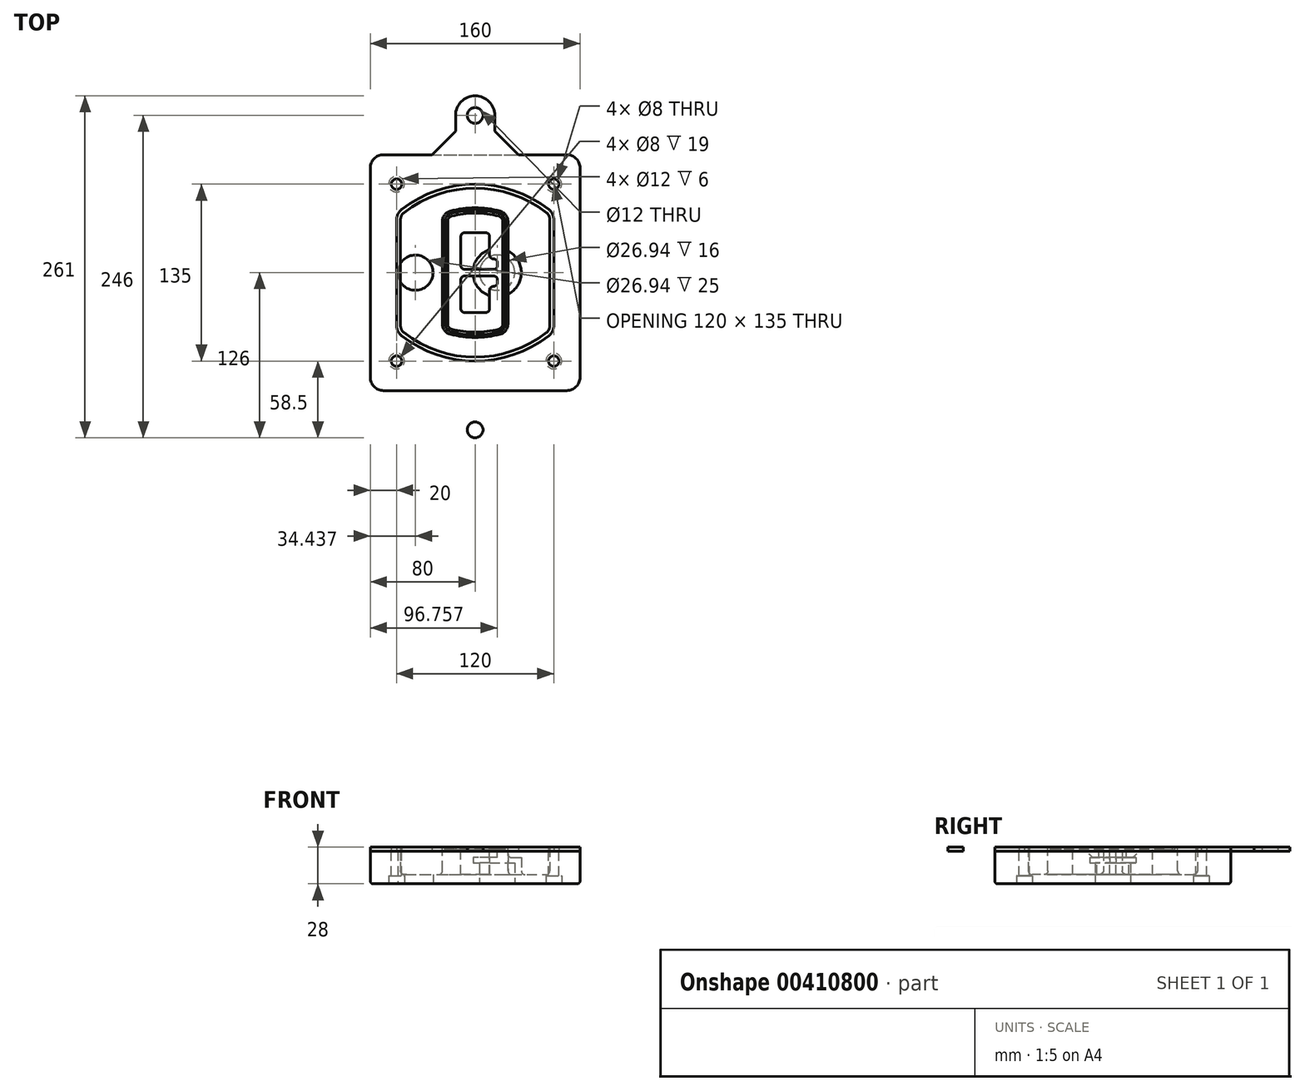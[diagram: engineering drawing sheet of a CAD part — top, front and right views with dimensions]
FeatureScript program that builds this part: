
annotation { "Feature Type Name" : "Feature", "Feature Type Description" : "" }
export const myFeature = defineFeature(function(context is Context, id is Id, definition is map)
    precondition{}
    {
        {
            var Q0;
            Q0=qCreatedBy(makeId("Top.planeOp"),FACE);
            var sketch = newSketch(context, id + "F0", { "sketchPlane" : qUnion([Q0])});
            skPoint(sketch, "E0.rect.middle", {"position": v(0, 0) * mm});
            skLineSegment(sketch, "E1.bottom", {"start": v(-70, -90) * mm, "end": v(70, -90) * mm});
            skLineSegment(sketch, "E1.top", {"start": v(-70, 90) * mm, "end": v(70, 90) * mm});
            skLineSegment(sketch, "E1.left", {"start": v(-80, -80) * mm, "end": v(-80, 80) * mm});
            skLineSegment(sketch, "E1.right", {"start": v(80, -80) * mm, "end": v(80, 80) * mm});
            skLineSegment(sketch, "E2", {"start": v(-80, 90) * mm, "end": v(80, -90) * mm, "construction": true});
            skLineSegment(sketch, "E3", {"start": v(80, 90) * mm, "end": v(-80, -90) * mm, "construction": true});
            skCircle(sketch, "E4", {"center": v(-60, 67.5) * mm, "radius": 4 * mm});
            skCircle(sketch, "E5", {"center": v(60, 67.5) * mm, "radius": 4 * mm});
            skCircle(sketch, "E6", {"center": v(60, -67.5) * mm, "radius": 4 * mm});
            skCircle(sketch, "E7", {"center": v(-60, -67.5) * mm, "radius": 4 * mm});
            skLineSegment(sketch, "E8", {"start": v(-60, 67.5) * mm, "end": v(60, 67.5) * mm, "construction": true});
            skLineSegment(sketch, "E9", {"start": v(60, 67.5) * mm, "end": v(60, -67.5) * mm, "construction": true});
            skLineSegment(sketch, "E10", {"start": v(60, -67.5) * mm, "end": v(-60, -67.5) * mm, "construction": true});
            skLineSegment(sketch, "E11", {"start": v(-60, -67.5) * mm, "end": v(-60, 67.5) * mm, "construction": true});
            skLineSegment(sketch, "E12", {"start": v(-60, 40.3) * mm, "end": v(-60, -40.3) * mm});
            skLineSegment(sketch, "E13", {"start": v(60, 40.3) * mm, "end": v(60, -40.3) * mm});
            skArc(sketch, "E14", {"start": v(56.15, 48.18) * mm, "mid": v(0, 67.5) * mm, "end": v(-56.15, 48.18) * mm});
            skArc(sketch, "E15", {"start": v(-56.15, -48.18) * mm, "mid": v(0, -67.5) * mm, "end": v(56.15, -48.18) * mm});
            skLineSegment(sketch, "E16", {"start": v(-60, 0) * mm, "end": v(60, 0) * mm, "construction": true});
            skPoint(sketch, "E17.visualSharp", {"position": v(-60, -45) * mm});
            skArc(sketch, "E17.filletArc", {"start": v(-60, -40.3) * mm, "mid": v(-58.99, -44.68) * mm, "end": v(-56.15, -48.18) * mm});
            skPoint(sketch, "E18.visualSharp", {"position": v(-60, 45) * mm});
            skArc(sketch, "E18.filletArc", {"start": v(-56.15, 48.18) * mm, "mid": v(-58.99, 44.68) * mm, "end": v(-60, 40.3) * mm});
            skPoint(sketch, "E19.visualSharp", {"position": v(60, 45) * mm});
            skArc(sketch, "E19.filletArc", {"start": v(60, 40.3) * mm, "mid": v(58.99, 44.68) * mm, "end": v(56.15, 48.18) * mm});
            skPoint(sketch, "E20.visualSharp", {"position": v(60, -45) * mm});
            skArc(sketch, "E20.filletArc", {"start": v(56.15, -48.18) * mm, "mid": v(58.99, -44.68) * mm, "end": v(60, -40.3) * mm});
            skPoint(sketch, "E21.visualSharp", {"position": v(-80, 90) * mm});
            skArc(sketch, "E21.filletArc", {"start": v(-70, 90) * mm, "mid": v(-77.07, 87.07) * mm, "end": v(-80, 80) * mm});
            skPoint(sketch, "E22.visualSharp", {"position": v(80, 90) * mm});
            skArc(sketch, "E22.filletArc", {"start": v(80, 80) * mm, "mid": v(77.07, 87.07) * mm, "end": v(70, 90) * mm});
            skPoint(sketch, "E23.visualSharp", {"position": v(80, -90) * mm});
            skArc(sketch, "E23.filletArc", {"start": v(70, -90) * mm, "mid": v(77.07, -87.07) * mm, "end": v(80, -80) * mm});
            skPoint(sketch, "E24.visualSharp", {"position": v(-80, -90) * mm});
            skArc(sketch, "E24.filletArc", {"start": v(-80, -80) * mm, "mid": v(-77.07, -87.07) * mm, "end": v(-70, -90) * mm});
            skArc(sketch, "E25.0", {"start": v(57, 40.3) * mm, "mid": v(56.3, 43.36) * mm, "end": v(54.3, 45.81) * mm});
            skLineSegment(sketch, "E25.1", {"start": v(57, 40.3) * mm, "end": v(57, -40.3) * mm});
            skArc(sketch, "E25.2", {"start": v(54.3, -45.81) * mm, "mid": v(56.3, -43.36) * mm, "end": v(57, -40.3) * mm});
            skArc(sketch, "E25.3", {"start": v(-54.3, -45.81) * mm, "mid": v(0, -64.5) * mm, "end": v(54.3, -45.81) * mm});
            skArc(sketch, "E25.4", {"start": v(-57, -40.3) * mm, "mid": v(-56.3, -43.36) * mm, "end": v(-54.3, -45.81) * mm});
            skArc(sketch, "E25.5", {"start": v(54.3, 45.81) * mm, "mid": v(0, 64.5) * mm, "end": v(-54.3, 45.81) * mm});
            skLineSegment(sketch, "E25.6", {"start": v(-57, 40.3) * mm, "end": v(-57, -40.3) * mm});
            skArc(sketch, "E25.7", {"start": v(-54.3, 45.81) * mm, "mid": v(-56.3, 43.36) * mm, "end": v(-57, 40.3) * mm});
            skArc(sketch, "E26.0", {"start": v(-58.62, 51.33) * mm, "mid": v(-62.58, 46.43) * mm, "end": v(-64, 40.3) * mm});
            skArc(sketch, "E26.1", {"start": v(58.62, 51.33) * mm, "mid": v(0, 71.5) * mm, "end": v(-58.62, 51.33) * mm});
            skArc(sketch, "E26.2", {"start": v(64, 40.3) * mm, "mid": v(62.58, 46.43) * mm, "end": v(58.62, 51.33) * mm});
            skLineSegment(sketch, "E26.3", {"start": v(64, 40.3) * mm, "end": v(64, -40.3) * mm});
            skArc(sketch, "E26.4", {"start": v(58.62, -51.33) * mm, "mid": v(62.58, -46.43) * mm, "end": v(64, -40.3) * mm});
            skLineSegment(sketch, "E26.5", {"start": v(-64, 40.3) * mm, "end": v(-64, -40.3) * mm});
            skArc(sketch, "E26.6", {"start": v(-58.62, -51.33) * mm, "mid": v(0, -71.5) * mm, "end": v(58.62, -51.33) * mm});
            skArc(sketch, "E26.7", {"start": v(-64, -40.3) * mm, "mid": v(-62.58, -46.43) * mm, "end": v(-58.62, -51.33) * mm});
            skSolve(sketch);
        }
        {
            var Q0;
            Q0=makeQuery(id+"F0.imprint","IMPRINT",FACE,{"disambiguationData":[TD([[makeQuery(id+"F0.imprint","IMPRINT",EDGE,{"derivedFrom":sQuery(id+"F0.wireOp",EDGE,"E1.bottom")}),1.0]])]});
            var Q1;
            Q1=makeQuery(id+"F0.imprint","IMPRINT",FACE,{"disambiguationData":[TD([[makeQuery(id+"F0.imprint","IMPRINT",EDGE,{"derivedFrom":sQuery(id+"F0.wireOp",EDGE,"E12")}),1.0]])]});
            var Q2;
            Q2=makeQuery(id+"F0.imprint","IMPRINT",FACE,{"disambiguationData":[TD([[makeQuery(id+"F0.imprint","IMPRINT",EDGE,{"derivedFrom":sQuery(id+"F0.wireOp",EDGE,"E25.0")}),1.0]])]});
            var Q3;
            Q3=makeQuery(id+"F0.imprint","IMPRINT",FACE,{"disambiguationData":[TD([[makeQuery(id+"F0.imprint","IMPRINT",EDGE,{"derivedFrom":sQuery(id+"F0.wireOp",EDGE,"E12")}),-1.0]])]});
            extrude(context, id + "F1", {"entities" : qUnion([Q0, Q1, Q2, Q3]), "oppositeDirection" : true, "depth" : 25 * mm});
        }
        {
            var Q0;
            Q0=makeQuery(id+"F0.imprint","IMPRINT",FACE,{"disambiguationData":[TD([[makeQuery(id+"F0.imprint","IMPRINT",EDGE,{"derivedFrom":sQuery(id+"F0.wireOp",EDGE,"E12")}),1.0]])]});
            extrude(context, id + "F2", {"entities" : qUnion([Q0]), "operationType" : NewBodyOperationType.ADD, "depth" : 3 * mm});
        }
        {
            var Q0;
            Q0=makeQuery(id+"F0.imprint","IMPRINT",FACE,{"disambiguationData":[TD([[makeQuery(id+"F0.imprint","IMPRINT",EDGE,{"derivedFrom":sQuery(id+"F0.wireOp",EDGE,"E25.0")}),1.0]])]});
            extrude(context, id + "F3", {"entities" : qUnion([Q0]), "operationType" : NewBodyOperationType.REMOVE, "oppositeDirection" : true, "depth" : 18 * mm});
        }
        {
            var Q0;
            Q0=makeQuery(id+"F2.opExtrude","CAP_FACE",FACE,{"disambiguationData":[OSD([sQuery(id+"F0.wireOp",EDGE,"E12"),sQuery(id+"F0.wireOp",EDGE,"E13"),sQuery(id+"F0.wireOp",EDGE,"E14"),sQuery(id+"F0.wireOp",EDGE,"E15"),sQuery(id+"F0.wireOp",EDGE,"E17.filletArc"),sQuery(id+"F0.wireOp",EDGE,"E18.filletArc"),sQuery(id+"F0.wireOp",EDGE,"E19.filletArc"),sQuery(id+"F0.wireOp",EDGE,"E20.filletArc"),sQuery(id+"F0.wireOp",EDGE,"E25.0"),sQuery(id+"F0.wireOp",EDGE,"E25.1"),sQuery(id+"F0.wireOp",EDGE,"E25.2"),sQuery(id+"F0.wireOp",EDGE,"E25.3"),sQuery(id+"F0.wireOp",EDGE,"E25.4"),sQuery(id+"F0.wireOp",EDGE,"E25.5"),sQuery(id+"F0.wireOp",EDGE,"E25.6"),sQuery(id+"F0.wireOp",EDGE,"E25.7")])],"isStart":false});
            var sketch = newSketch(context, id + "F4", { "sketchPlane" : qUnion([Q0])});
            skArc(sketch, "E27.0", {"start": v(-19.08, -46.97) * mm, "mid": v(0, -49.5) * mm, "end": v(19.08, -46.97) * mm});
            skArc(sketch, "E28.0", {"start": v(19.08, 46.97) * mm, "mid": v(0, 49.5) * mm, "end": v(-19.08, 46.97) * mm});
            skLineSegment(sketch, "E29", {"start": v(-25, 39.25) * mm, "end": v(-25, -39.25) * mm});
            skLineSegment(sketch, "E30", {"start": v(25, 39.25) * mm, "end": v(25, -39.25) * mm});
            skLineSegment(sketch, "E31", {"start": v(-25, 45.1) * mm, "end": v(25, 45.1) * mm, "construction": true});
            skLineSegment(sketch, "E32", {"start": v(-25, -45.1) * mm, "end": v(25, -45.1) * mm, "construction": true});
            skPoint(sketch, "E33.visualSharp", {"position": v(-25, 45.1) * mm});
            skArc(sketch, "E33.filletArc", {"start": v(-19.08, 46.97) * mm, "mid": v(-23.35, 44.11) * mm, "end": v(-25, 39.25) * mm});
            skPoint(sketch, "E34.visualSharp", {"position": v(25, 45.1) * mm});
            skArc(sketch, "E34.filletArc", {"start": v(25, 39.25) * mm, "mid": v(23.35, 44.11) * mm, "end": v(19.08, 46.97) * mm});
            skPoint(sketch, "E35.visualSharp", {"position": v(25, -45.1) * mm});
            skArc(sketch, "E35.filletArc", {"start": v(19.08, -46.97) * mm, "mid": v(23.35, -44.11) * mm, "end": v(25, -39.25) * mm});
            skPoint(sketch, "E36.visualSharp", {"position": v(-25, -45.1) * mm});
            skArc(sketch, "E36.filletArc", {"start": v(-25, -39.25) * mm, "mid": v(-23.35, -44.11) * mm, "end": v(-19.08, -46.97) * mm});
            skArc(sketch, "E37.0", {"start": v(54.3, 45.81) * mm, "mid": v(0, 64.5) * mm, "end": v(-54.3, 45.81) * mm});
            skArc(sketch, "E37.1", {"start": v(-54.3, 45.81) * mm, "mid": v(-56.3, 43.36) * mm, "end": v(-57, 40.3) * mm});
            skLineSegment(sketch, "E37.2", {"start": v(-57, 40.3) * mm, "end": v(-57, -40.3) * mm});
            skArc(sketch, "E37.3", {"start": v(-57, -40.3) * mm, "mid": v(-56.3, -43.36) * mm, "end": v(-54.3, -45.81) * mm});
            skArc(sketch, "E37.4", {"start": v(-54.3, -45.81) * mm, "mid": v(0, -64.5) * mm, "end": v(54.3, -45.81) * mm});
            skArc(sketch, "E37.5", {"start": v(54.3, -45.81) * mm, "mid": v(56.3, -43.36) * mm, "end": v(57, -40.3) * mm});
            skLineSegment(sketch, "E37.6", {"start": v(57, 40.3) * mm, "end": v(57, -40.3) * mm});
            skArc(sketch, "E37.7", {"start": v(57, 40.3) * mm, "mid": v(56.3, 43.36) * mm, "end": v(54.3, 45.81) * mm});
            skLineSegment(sketch, "E38.0", {"start": v(23, 39.25) * mm, "end": v(23, -39.25) * mm});
            skArc(sketch, "E38.1", {"start": v(18.56, -45.04) * mm, "mid": v(21.76, -42.9) * mm, "end": v(23, -39.25) * mm});
            skArc(sketch, "E38.2", {"start": v(-18.56, -45.04) * mm, "mid": v(0, -47.5) * mm, "end": v(18.56, -45.04) * mm});
            skArc(sketch, "E38.3", {"start": v(-23, -39.25) * mm, "mid": v(-21.76, -42.9) * mm, "end": v(-18.56, -45.04) * mm});
            skLineSegment(sketch, "E38.4", {"start": v(-23, 39.25) * mm, "end": v(-23, -39.25) * mm});
            skArc(sketch, "E38.5", {"start": v(23, 39.25) * mm, "mid": v(21.76, 42.9) * mm, "end": v(18.56, 45.04) * mm});
            skArc(sketch, "E38.6", {"start": v(-18.56, 45.04) * mm, "mid": v(-21.76, 42.9) * mm, "end": v(-23, 39.25) * mm});
            skArc(sketch, "E38.7", {"start": v(18.56, 45.04) * mm, "mid": v(0, 47.5) * mm, "end": v(-18.56, 45.04) * mm});
            skArc(sketch, "E39.0", {"start": v(21, 39.25) * mm, "mid": v(20.18, 41.68) * mm, "end": v(18.04, 43.1) * mm});
            skLineSegment(sketch, "E39.1", {"start": v(21, 39.25) * mm, "end": v(21, -39.25) * mm});
            skArc(sketch, "E39.2", {"start": v(18.04, -43.1) * mm, "mid": v(20.18, -41.68) * mm, "end": v(21, -39.25) * mm});
            skArc(sketch, "E39.3", {"start": v(-18.04, -43.1) * mm, "mid": v(0, -45.5) * mm, "end": v(18.04, -43.1) * mm});
            skArc(sketch, "E39.4", {"start": v(-21, -39.25) * mm, "mid": v(-20.18, -41.68) * mm, "end": v(-18.04, -43.1) * mm});
            skArc(sketch, "E39.5", {"start": v(18.04, 43.1) * mm, "mid": v(0, 45.5) * mm, "end": v(-18.04, 43.1) * mm});
            skLineSegment(sketch, "E39.6", {"start": v(-21, 39.25) * mm, "end": v(-21, -39.25) * mm});
            skArc(sketch, "E39.7", {"start": v(-18.04, 43.1) * mm, "mid": v(-20.18, 41.68) * mm, "end": v(-21, 39.25) * mm});
            skLineSegment(sketch, "E40", {"start": v(-25, 0) * mm, "end": v(25, 0) * mm, "construction": true});
            skLineSegment(sketch, "E41", {"start": v(-11, 5.5) * mm, "end": v(-11, 27.5) * mm});
            skLineSegment(sketch, "E42", {"start": v(-8, 30.5) * mm, "end": v(8, 30.5) * mm});
            skLineSegment(sketch, "E43", {"start": v(11, 27.5) * mm, "end": v(11, 13.5) * mm});
            skLineSegment(sketch, "E44", {"start": v(14, 10.5) * mm, "end": v(14, 10.5) * mm});
            skLineSegment(sketch, "E45", {"start": v(17, 7.5) * mm, "end": v(17, 5.5) * mm});
            skLineSegment(sketch, "E46", {"start": v(14, 2.5) * mm, "end": v(-8, 2.5) * mm});
            skPoint(sketch, "E47.visualSharp", {"position": v(-11, 30.5) * mm});
            skArc(sketch, "E47.filletArc", {"start": v(-8, 30.5) * mm, "mid": v(-10.12, 29.62) * mm, "end": v(-11, 27.5) * mm});
            skPoint(sketch, "E48.visualSharp", {"position": v(11, 30.5) * mm});
            skArc(sketch, "E48.filletArc", {"start": v(11, 27.5) * mm, "mid": v(10.12, 29.62) * mm, "end": v(8, 30.5) * mm});
            skPoint(sketch, "E49.visualSharp", {"position": v(11, 10.5) * mm});
            skArc(sketch, "E49.filletArc", {"start": v(11, 13.5) * mm, "mid": v(11.88, 11.38) * mm, "end": v(14, 10.5) * mm});
            skPoint(sketch, "E50.visualSharp", {"position": v(17, 10.5) * mm});
            skArc(sketch, "E50.filletArc", {"start": v(17, 7.5) * mm, "mid": v(16.12, 9.62) * mm, "end": v(14, 10.5) * mm});
            skPoint(sketch, "E51.visualSharp", {"position": v(17, 2.5) * mm});
            skArc(sketch, "E51.filletArc", {"start": v(14, 2.5) * mm, "mid": v(16.12, 3.38) * mm, "end": v(17, 5.5) * mm});
            skPoint(sketch, "E52.visualSharp", {"position": v(-11, 2.5) * mm});
            skArc(sketch, "E52.filletArc", {"start": v(-11, 5.5) * mm, "mid": v(-10.12, 3.38) * mm, "end": v(-8, 2.5) * mm});
            skLineSegment(sketch, "E53.0.MirrorCS", {"start": v(14, -2.5) * mm, "end": v(-8, -2.5) * mm});
            skArc(sketch, "E54.0.MirrorCS", {"start": v(-11, -5.5) * mm, "mid": v(-10.12, -3.38) * mm, "end": v(-8, -2.5) * mm});
            skLineSegment(sketch, "E55.0.MirrorCS", {"start": v(-11, -5.5) * mm, "end": v(-11, -27.5) * mm});
            skArc(sketch, "E56.0.MirrorCS", {"start": v(-8, -30.5) * mm, "mid": v(-10.12, -29.62) * mm, "end": v(-11, -27.5) * mm});
            skLineSegment(sketch, "E57.0.MirrorCS", {"start": v(-8, -30.5) * mm, "end": v(8, -30.5) * mm});
            skArc(sketch, "E58.0.MirrorCS", {"start": v(11, -27.5) * mm, "mid": v(10.12, -29.62) * mm, "end": v(8, -30.5) * mm});
            skLineSegment(sketch, "E59.0.MirrorCS", {"start": v(11, -27.5) * mm, "end": v(11, -13.5) * mm});
            skArc(sketch, "E60.0.MirrorCS", {"start": v(11, -13.5) * mm, "mid": v(11.88, -11.38) * mm, "end": v(14, -10.5) * mm});
            skArc(sketch, "E61.0.MirrorCS", {"start": v(17, -7.5) * mm, "mid": v(16.12, -9.62) * mm, "end": v(14, -10.5) * mm});
            skLineSegment(sketch, "E62.0.MirrorCS", {"start": v(17, -7.5) * mm, "end": v(17, -5.5) * mm});
            skArc(sketch, "E63.0.MirrorCS", {"start": v(14, -2.5) * mm, "mid": v(16.12, -3.38) * mm, "end": v(17, -5.5) * mm});
            skSolve(sketch);
        }
        {
            var Q0;
            Q0=makeQuery(id+"F4.imprint","IMPRINT",FACE,{"disambiguationData":[TD([[makeQuery(id+"F4.imprint","IMPRINT",EDGE,{"derivedFrom":sQuery(id+"F4.wireOp",EDGE,"E27.0")}),1.0]])]});
            var Q1;
            Q1=makeQuery(id+"F4.imprint","IMPRINT",FACE,{"disambiguationData":[TD([[makeQuery(id+"F4.imprint","IMPRINT",EDGE,{"derivedFrom":sQuery(id+"F4.wireOp",EDGE,"E38.0")}),-1.0]])]});
            var Q2;
            Q2=makeQuery(id+"F4.imprint","IMPRINT",FACE,{"disambiguationData":[TD([[makeQuery(id+"F4.imprint","IMPRINT",EDGE,{"derivedFrom":sQuery(id+"F4.wireOp",EDGE,"E39.0")}),1.0]])]});
            extrude(context, id + "F5", {"entities" : qUnion([Q0, Q1, Q2]), "operationType" : NewBodyOperationType.ADD, "endBound" : BoundingType.UP_TO_NEXT, "oppositeDirection" : true, "depth" : 25 * mm});
        }
        {
            var Q0;
            Q0=makeQuery(id+"F4.imprint","IMPRINT",FACE,{"disambiguationData":[TD([[makeQuery(id+"F4.imprint","IMPRINT",EDGE,{"derivedFrom":sQuery(id+"F4.wireOp",EDGE,"E38.0")}),-1.0]])]});
            extrude(context, id + "F6", {"entities" : qUnion([Q0]), "operationType" : NewBodyOperationType.REMOVE, "oppositeDirection" : true, "depth" : 2 * mm});
        }
        {
            var Q0;
            Q0=makeQuery(id+"F1.opExtrude","CAP_FACE",FACE,{"disambiguationData":[OSD([sQuery(id+"F0.wireOp",EDGE,"E1.bottom"),sQuery(id+"F0.wireOp",EDGE,"E1.top"),sQuery(id+"F0.wireOp",EDGE,"E1.left"),sQuery(id+"F0.wireOp",EDGE,"E1.right"),sQuery(id+"F0.wireOp",EDGE,"E4"),sQuery(id+"F0.wireOp",EDGE,"E5"),sQuery(id+"F0.wireOp",EDGE,"E6"),sQuery(id+"F0.wireOp",EDGE,"E7"),sQuery(id+"F0.wireOp",EDGE,"E21.filletArc"),sQuery(id+"F0.wireOp",EDGE,"E22.filletArc"),sQuery(id+"F0.wireOp",EDGE,"E23.filletArc"),sQuery(id+"F0.wireOp",EDGE,"E24.filletArc")])],"isStart":false});
            var sketch = newSketch(context, id + "F7", { "sketchPlane" : qUnion([Q0])});
            skCircle(sketch, "E64", {"center": v(16.76, 0) * mm, "radius": 13.47 * mm});
            skCircle(sketch, "E65", {"center": v(-45.56, 0) * mm, "radius": 13.47 * mm});
            skLineSegment(sketch, "E66", {"start": v(80, 0) * mm, "end": v(-80, 0) * mm});
            skCircle(sketch, "E67", {"center": v(16.76, 0) * mm, "radius": 18.47 * mm});
            skCircle(sketch, "E68", {"center": v(60, -67.5) * mm, "radius": 6 * mm});
            skCircle(sketch, "E69", {"center": v(-60, -67.5) * mm, "radius": 6 * mm});
            skCircle(sketch, "E70", {"center": v(-60, 67.5) * mm, "radius": 6 * mm});
            skCircle(sketch, "E71", {"center": v(60, 67.5) * mm, "radius": 6 * mm});
            skSolve(sketch);
        }
        {
            var Q0;
            {var subQ1=sQuery(id+"F7.wireOp",EDGE,"E66");var subQ4=sQuery(id+"F7.wireOp",EDGE,"E64");var subQ6=makeQuery(id+"F7.imprint","INTERSECT",VERTEX,{"disambiguationData":[OD(0.0)],"derivedFrom":[subQ4,subQ1]});Q0=makeQuery(id+"F7.imprint","IMPRINT",FACE,{"disambiguationData":[TD([[makeQuery(id+"F7.imprint","IMPRINT",EDGE,{"disambiguationData":[TD([[subQ6,-1.0]])],"derivedFrom":subQ4}),-1.0]])]});}
            var Q1;
            {var subQ0=sQuery(id+"F7.wireOp",EDGE,"E66");var subQ1=sQuery(id+"F7.wireOp",EDGE,"E64");var subQ3=makeQuery(id+"F7.imprint","INTERSECT",VERTEX,{"disambiguationData":[OD(0.0)],"derivedFrom":[subQ1,subQ0]});Q1=makeQuery(id+"F7.imprint","IMPRINT",FACE,{"disambiguationData":[TD([[makeQuery(id+"F7.imprint","IMPRINT",EDGE,{"disambiguationData":[TD([[subQ3,-1.0]])],"derivedFrom":subQ1}),1.0]])]});}
            var Q2;
            {var subQ0=sQuery(id+"F7.wireOp",EDGE,"E66");var subQ1=sQuery(id+"F7.wireOp",EDGE,"E64");var subQ3=makeQuery(id+"F7.imprint","INTERSECT",VERTEX,{"disambiguationData":[OD(0.0)],"derivedFrom":[subQ1,subQ0]});Q2=makeQuery(id+"F7.imprint","IMPRINT",FACE,{"disambiguationData":[TD([[makeQuery(id+"F7.imprint","IMPRINT",EDGE,{"disambiguationData":[TD([[subQ3,1.0]])],"derivedFrom":subQ1}),1.0]])]});}
            var Q3;
            {var subQ1=sQuery(id+"F7.wireOp",EDGE,"E66");var subQ4=sQuery(id+"F7.wireOp",EDGE,"E64");var subQ6=makeQuery(id+"F7.imprint","INTERSECT",VERTEX,{"disambiguationData":[OD(0.0)],"derivedFrom":[subQ4,subQ1]});Q3=makeQuery(id+"F7.imprint","IMPRINT",FACE,{"disambiguationData":[TD([[makeQuery(id+"F7.imprint","IMPRINT",EDGE,{"disambiguationData":[TD([[subQ6,1.0]])],"derivedFrom":subQ4}),-1.0]])]});}
            extrude(context, id + "F8", {"entities" : qUnion([Q0, Q1, Q2, Q3]), "operationType" : NewBodyOperationType.ADD, "oppositeDirection" : true, "depth" : 20 * mm});
        }
        {
            var Q0;
            {var subQ0=sQuery(id+"F7.wireOp",EDGE,"E66");var subQ1=sQuery(id+"F7.wireOp",EDGE,"E64");var subQ3=makeQuery(id+"F7.imprint","INTERSECT",VERTEX,{"disambiguationData":[OD(0.0)],"derivedFrom":[subQ1,subQ0]});Q0=makeQuery(id+"F7.imprint","IMPRINT",FACE,{"disambiguationData":[TD([[makeQuery(id+"F7.imprint","IMPRINT",EDGE,{"disambiguationData":[TD([[subQ3,-1.0]])],"derivedFrom":subQ1}),1.0]])]});}
            var Q1;
            {var subQ0=sQuery(id+"F7.wireOp",EDGE,"E66");var subQ1=sQuery(id+"F7.wireOp",EDGE,"E64");var subQ3=makeQuery(id+"F7.imprint","INTERSECT",VERTEX,{"disambiguationData":[OD(0.0)],"derivedFrom":[subQ1,subQ0]});Q1=makeQuery(id+"F7.imprint","IMPRINT",FACE,{"disambiguationData":[TD([[makeQuery(id+"F7.imprint","IMPRINT",EDGE,{"disambiguationData":[TD([[subQ3,1.0]])],"derivedFrom":subQ1}),1.0]])]});}
            extrude(context, id + "F9", {"entities" : qUnion([Q0, Q1]), "operationType" : NewBodyOperationType.REMOVE, "oppositeDirection" : true, "depth" : 16 * mm});
        }
        {
            var Q0;
            {var subQ0=sQuery(id+"F7.wireOp",EDGE,"E66");var subQ1=sQuery(id+"F7.wireOp",EDGE,"E65");var subQ3=makeQuery(id+"F7.imprint","INTERSECT",VERTEX,{"disambiguationData":[OD(0.0)],"derivedFrom":[subQ1,subQ0]});Q0=makeQuery(id+"F7.imprint","IMPRINT",FACE,{"disambiguationData":[TD([[makeQuery(id+"F7.imprint","IMPRINT",EDGE,{"disambiguationData":[TD([[subQ3,-1.0]])],"derivedFrom":subQ1}),1.0]])]});}
            var Q1;
            {var subQ0=sQuery(id+"F7.wireOp",EDGE,"E66");var subQ1=sQuery(id+"F7.wireOp",EDGE,"E65");var subQ3=makeQuery(id+"F7.imprint","INTERSECT",VERTEX,{"disambiguationData":[OD(0.0)],"derivedFrom":[subQ1,subQ0]});Q1=makeQuery(id+"F7.imprint","IMPRINT",FACE,{"disambiguationData":[TD([[makeQuery(id+"F7.imprint","IMPRINT",EDGE,{"disambiguationData":[TD([[subQ3,1.0]])],"derivedFrom":subQ1}),1.0]])]});}
            extrude(context, id + "F10", {"entities" : qUnion([Q0, Q1]), "operationType" : NewBodyOperationType.REMOVE, "oppositeDirection" : true, "depth" : 25 * mm});
        }
        {
            var Q0;
            Q0=makeQuery(id+"F7.imprint","IMPRINT",FACE,{"disambiguationData":[TD([[makeQuery(id+"F7.imprint","IMPRINT",EDGE,{"derivedFrom":sQuery(id+"F7.wireOp",EDGE,"E68")}),1.0]])]});
            var Q1;
            Q1=makeQuery(id+"F7.imprint","IMPRINT",FACE,{"disambiguationData":[TD([[makeQuery(id+"F7.imprint","IMPRINT",EDGE,{"derivedFrom":makeQuery(id+"F1.opExtrude","CAP_EDGE",EDGE,{"disambiguationData":[OSD([sQuery(id+"F0.wireOp",EDGE,"E5")])],"isStart":false})}),-1.0]])]});
            var Q2;
            Q2=makeQuery(id+"F7.imprint","IMPRINT",FACE,{"disambiguationData":[TD([[makeQuery(id+"F7.imprint","IMPRINT",EDGE,{"derivedFrom":sQuery(id+"F7.wireOp",EDGE,"E69")}),1.0]])]});
            var Q3;
            Q3=makeQuery(id+"F7.imprint","IMPRINT",FACE,{"disambiguationData":[TD([[makeQuery(id+"F7.imprint","IMPRINT",EDGE,{"derivedFrom":makeQuery(id+"F1.opExtrude","CAP_EDGE",EDGE,{"disambiguationData":[OSD([sQuery(id+"F0.wireOp",EDGE,"E4")])],"isStart":false})}),-1.0]])]});
            var Q4;
            Q4=makeQuery(id+"F7.imprint","IMPRINT",FACE,{"disambiguationData":[TD([[makeQuery(id+"F7.imprint","IMPRINT",EDGE,{"derivedFrom":sQuery(id+"F7.wireOp",EDGE,"E70")}),1.0]])]});
            var Q5;
            Q5=makeQuery(id+"F7.imprint","IMPRINT",FACE,{"disambiguationData":[TD([[makeQuery(id+"F7.imprint","IMPRINT",EDGE,{"derivedFrom":makeQuery(id+"F1.opExtrude","CAP_EDGE",EDGE,{"disambiguationData":[OSD([sQuery(id+"F0.wireOp",EDGE,"E7")])],"isStart":false})}),-1.0]])]});
            var Q6;
            Q6=makeQuery(id+"F7.imprint","IMPRINT",FACE,{"disambiguationData":[TD([[makeQuery(id+"F7.imprint","IMPRINT",EDGE,{"derivedFrom":sQuery(id+"F7.wireOp",EDGE,"E71")}),1.0]])]});
            var Q7;
            Q7=makeQuery(id+"F7.imprint","IMPRINT",FACE,{"disambiguationData":[TD([[makeQuery(id+"F7.imprint","IMPRINT",EDGE,{"derivedFrom":makeQuery(id+"F1.opExtrude","CAP_EDGE",EDGE,{"disambiguationData":[OSD([sQuery(id+"F0.wireOp",EDGE,"E6")])],"isStart":false})}),-1.0]])]});
            extrude(context, id + "F11", {"entities" : qUnion([Q0, Q1, Q2, Q3, Q4, Q5, Q6, Q7]), "operationType" : NewBodyOperationType.REMOVE, "oppositeDirection" : true, "depth" : 6 * mm});
        }
        {
            var Q0;
            Q0=makeQuery(id+"F9.boolean.opBoolean","COPY",FACE,{"derivedFrom":makeQuery(id+"F9.opExtrude","CAP_FACE",FACE,{"disambiguationData":[OSD([sQuery(id+"F7.wireOp",EDGE,"E64")])],"isStart":false})});
            var sketch = newSketch(context, id + "F12", { "sketchPlane" : qUnion([Q0])});
            skArc(sketch, "E72.0", {"start": v(11, 17.55) * mm, "mid": v(2.57, 11.82) * mm, "end": v(-1.54, 2.5) * mm});
            skArc(sketch, "E72.1", {"start": v(-1.54, -2.5) * mm, "mid": v(2.57, -11.82) * mm, "end": v(11, -17.55) * mm});
            skLineSegment(sketch, "E73", {"start": v(-1.54, -2.5) * mm, "end": v(14, -2.5) * mm});
            skLineSegment(sketch, "E74.0", {"start": v(14, 2.5) * mm, "end": v(-1.54, 2.5) * mm});
            skArc(sketch, "E74.1", {"start": v(14, 2.5) * mm, "mid": v(16.12, 3.38) * mm, "end": v(17, 5.5) * mm});
            skLineSegment(sketch, "E74.2", {"start": v(17, 7.5) * mm, "end": v(17, 5.5) * mm});
            skArc(sketch, "E74.3", {"start": v(17, 7.5) * mm, "mid": v(16.12, 9.62) * mm, "end": v(14, 10.5) * mm});
            skArc(sketch, "E74.4", {"start": v(11, 13.5) * mm, "mid": v(11.88, 11.38) * mm, "end": v(14, 10.5) * mm});
            skLineSegment(sketch, "E74.5", {"start": v(11, 17.55) * mm, "end": v(11, 13.5) * mm});
            skLineSegment(sketch, "E74.7", {"start": v(14, -2.5) * mm, "end": v(-1.54, -2.5) * mm});
            skArc(sketch, "E74.8", {"start": v(14, -2.5) * mm, "mid": v(16.12, -3.38) * mm, "end": v(17, -5.5) * mm});
            skLineSegment(sketch, "E74.9", {"start": v(17, -7.5) * mm, "end": v(17, -5.5) * mm});
            skArc(sketch, "E74.10", {"start": v(17, -7.5) * mm, "mid": v(16.12, -9.62) * mm, "end": v(14, -10.5) * mm});
            skArc(sketch, "E74.11", {"start": v(11, -13.5) * mm, "mid": v(11.88, -11.38) * mm, "end": v(14, -10.5) * mm});
            skLineSegment(sketch, "E74.12", {"start": v(11, -17.55) * mm, "end": v(11, -13.5) * mm});
            skPoint(sketch, "E75.orphan", {"position": v(11, -27.5) * mm});
            skPoint(sketch, "E76.orphan", {"position": v(-8, -2.5) * mm});
            skPoint(sketch, "E77.orphan", {"position": v(-8, 2.5) * mm});
            skPoint(sketch, "E78.orphan", {"position": v(11, 27.5) * mm});
            skSolve(sketch);
        }
        {
            var Q0;
            {var subQ7=sQuery(id+"F12.wireOp",EDGE,"E72.0");var subQ14=sQuery(id+"F12.wireOp",EDGE,"E72.1");var subQ16=sQuery(id+"F12.wireOp",EDGE,"E74.1");var subQ18=sQuery(id+"F12.wireOp",EDGE,"E74.8");Q0=qUnion([makeQuery(id+"F12.imprint","IMPRINT",FACE,{"disambiguationData":[TD([[makeQuery(id+"F12.imprint","IMPRINT",EDGE,{"derivedFrom":subQ7}),1.0]])]}),makeQuery(id+"F12.imprint","IMPRINT",FACE,{"disambiguationData":[TD([[makeQuery(id+"F12.imprint","IMPRINT",EDGE,{"derivedFrom":subQ14}),1.0]])]}),makeQuery(id+"F12.imprint","IMPRINT",FACE,{"disambiguationData":[TD([[makeQuery(id+"F12.imprint","IMPRINT",EDGE,{"derivedFrom":subQ16}),1.0]])]}),makeQuery(id+"F12.imprint","IMPRINT",FACE,{"disambiguationData":[TD([[makeQuery(id+"F12.imprint","IMPRINT",EDGE,{"derivedFrom":subQ18}),-1.0]])]})]);}
            var Q1;
            Q1=makeQuery(id+"F5.boolean.opBoolean","SPLIT",FACE,{"disambiguationData":[TD([makeQuery(id+"F5.opExtrude","SWEPT_FACE",FACE,{"disambiguationData":[OSD([sQuery(id+"F4.wireOp",EDGE,"E41")])]})])],"derivedFrom":makeQuery(id+"F3.boolean.opBoolean","COPY",FACE,{"derivedFrom":makeQuery(id+"F3.opExtrude","CAP_FACE",FACE,{"disambiguationData":[OSD([sQuery(id+"F0.wireOp",EDGE,"E25.0"),sQuery(id+"F0.wireOp",EDGE,"E25.1"),sQuery(id+"F0.wireOp",EDGE,"E25.2"),sQuery(id+"F0.wireOp",EDGE,"E25.3"),sQuery(id+"F0.wireOp",EDGE,"E25.4"),sQuery(id+"F0.wireOp",EDGE,"E25.5"),sQuery(id+"F0.wireOp",EDGE,"E25.6"),sQuery(id+"F0.wireOp",EDGE,"E25.7")])],"isStart":false})})});
            extrude(context, id + "F13", {"entities" : qUnion([Q0]), "operationType" : NewBodyOperationType.REMOVE, "endBound" : BoundingType.UP_TO_SURFACE, "endBoundEntityFace" : qUnion([Q1]), "depth" : 25 * mm});
        }
        {
            var Q0;
            Q0=makeQuery(id+"F3.boolean.opBoolean","COPY",EDGE,{"derivedFrom":makeQuery(id+"F3.opExtrude","CAP_EDGE",EDGE,{"disambiguationData":[OSD([sQuery(id+"F0.wireOp",EDGE,"E25.6")])],"isStart":false})});
            var Q1;
            Q1=makeQuery(id+"F8.boolean.opBoolean","INTERSECT",EDGE,{"derivedFrom":[makeQuery(id+"F5.opExtrude","SWEPT_FACE",FACE,{"disambiguationData":[OSD([sQuery(id+"F4.wireOp",EDGE,"E30")])]}),makeQuery(id+"F8.opExtrude","CAP_FACE",FACE,{"disambiguationData":[OSD([sQuery(id+"F7.wireOp",EDGE,"E67")])],"isStart":false})]});
            var Q2;
            Q2=makeQuery(id+"F8.boolean.opBoolean","INTERSECT",EDGE,{"disambiguationData":[OD(1.0)],"derivedFrom":[makeQuery(id+"F5.opExtrude","SWEPT_FACE",FACE,{"disambiguationData":[OSD([sQuery(id+"F4.wireOp",EDGE,"E30")])]}),makeQuery(id+"F8.opExtrude","SWEPT_FACE",FACE,{"disambiguationData":[OSD([sQuery(id+"F7.wireOp",EDGE,"E67")])]})]});
            var Q3;
            {var subQ0=sQuery(id+"F4.wireOp",EDGE,"E30");Q3=makeQuery(id+"F8.boolean.opBoolean","SPLIT",EDGE,{"disambiguationData":[TD([makeQuery(id+"F5.opExtrude","SWEPT_FACE",FACE,{"disambiguationData":[OSD([sQuery(id+"F4.wireOp",EDGE,"E35.filletArc")])]})])],"derivedFrom":makeQuery(id+"F5.opExtrude","CAP_EDGE",EDGE,{"disambiguationData":[OSD([subQ0])],"isStart":false})});}
            var Q4;
            {var subQ0=sQuery(id+"F0.wireOp",EDGE,"E25.7");var subQ1=sQuery(id+"F0.wireOp",EDGE,"E25.1");var subQ2=sQuery(id+"F0.wireOp",EDGE,"E25.6");var subQ3=sQuery(id+"F0.wireOp",EDGE,"E25.5");var subQ4=sQuery(id+"F0.wireOp",EDGE,"E25.4");var subQ5=sQuery(id+"F0.wireOp",EDGE,"E25.0");var subQ6=sQuery(id+"F0.wireOp",EDGE,"E25.2");var subQ7=sQuery(id+"F0.wireOp",EDGE,"E25.3");Q4=makeQuery(id+"F8.boolean.opBoolean","INTERSECT",EDGE,{"derivedFrom":[makeQuery(id+"F5.boolean.opBoolean","SPLIT",FACE,{"disambiguationData":[TD([makeQuery(id+"F2.opExtrude","SWEPT_FACE",FACE,{"disambiguationData":[OSD([subQ5])]})])],"derivedFrom":makeQuery(id+"F3.boolean.opBoolean","COPY",FACE,{"derivedFrom":makeQuery(id+"F3.opExtrude","CAP_FACE",FACE,{"disambiguationData":[OSD([subQ5,subQ1,subQ6,subQ7,subQ4,subQ3,subQ2,subQ0])],"isStart":false})})}),makeQuery(id+"F8.opExtrude","SWEPT_FACE",FACE,{"disambiguationData":[OSD([sQuery(id+"F7.wireOp",EDGE,"E67")])]})]});}
            var Q5;
            Q5=makeQuery(id+"F8.boolean.opBoolean","INTERSECT",EDGE,{"disambiguationData":[OD(0.0)],"derivedFrom":[makeQuery(id+"F5.opExtrude","SWEPT_FACE",FACE,{"disambiguationData":[OSD([sQuery(id+"F4.wireOp",EDGE,"E30")])]}),makeQuery(id+"F8.opExtrude","SWEPT_FACE",FACE,{"disambiguationData":[OSD([sQuery(id+"F7.wireOp",EDGE,"E67")])]})]});
            fillet(context, id + "F14", {"entities" : qUnion([Q0, Q1, Q2, Q3, Q4, Q5]), "radius" : 3 * mm, "tangentPropagation" : true, "allowEdgeOverflow" : false});
        }
        {
            var Q0;
            Q0=makeQuery(id+"F1.opExtrude","CAP_EDGE",EDGE,{"disambiguationData":[OSD([sQuery(id+"F0.wireOp",EDGE,"E1.bottom")])],"isStart":false});
            fillet(context, id + "F15", {"entities" : qUnion([Q0]), "radius" : 2 * mm, "tangentPropagation" : true, "allowEdgeOverflow" : false});
        }
        {
            var Q0;
            {var subQ0=sQuery(id+"F0.wireOp",EDGE,"E21.filletArc");var subQ1=sQuery(id+"F0.wireOp",EDGE,"E7");var subQ2=sQuery(id+"F0.wireOp",EDGE,"E6");var subQ3=sQuery(id+"F0.wireOp",EDGE,"E5");var subQ4=sQuery(id+"F0.wireOp",EDGE,"E4");var subQ5=sQuery(id+"F0.wireOp",EDGE,"E22.filletArc");var subQ6=sQuery(id+"F0.wireOp",EDGE,"E1.bottom");var subQ7=sQuery(id+"F0.wireOp",EDGE,"E1.right");var subQ8=sQuery(id+"F0.wireOp",EDGE,"E1.top");var subQ9=sQuery(id+"F0.wireOp",EDGE,"E1.left");var subQ10=sQuery(id+"F0.wireOp",EDGE,"E23.filletArc");var subQ11=sQuery(id+"F0.wireOp",EDGE,"E24.filletArc");Q0=makeQuery(id+"F2.boolean.opBoolean","SPLIT",FACE,{"disambiguationData":[TD([makeQuery(id+"F1.opExtrude","SWEPT_FACE",FACE,{"disambiguationData":[OSD([subQ6])]})])],"derivedFrom":makeQuery(id+"F1.opExtrude","CAP_FACE",FACE,{"disambiguationData":[OSD([subQ6,subQ8,subQ9,subQ7,subQ4,subQ3,subQ2,subQ1,subQ0,subQ5,subQ10,subQ11])],"isStart":true})});}
            var sketch = newSketch(context, id + "F16", { "sketchPlane" : qUnion([Q0])});
            skLineSegment(sketch, "E79", {"start": v(0, 90) * mm, "end": v(0, 110.56) * mm, "construction": true});
            skLineSegment(sketch, "E80", {"start": v(-33, 90) * mm, "end": v(-15, 108) * mm});
            skLineSegment(sketch, "E81", {"start": v(-15, 108) * mm, "end": v(-15, 120) * mm});
            skLineSegment(sketch, "E82", {"start": v(33, 90) * mm, "end": v(15, 108) * mm});
            skLineSegment(sketch, "E83", {"start": v(15, 108) * mm, "end": v(15, 120) * mm});
            skArc(sketch, "E84", {"start": v(15, 120) * mm, "mid": v(0, 135) * mm, "end": v(-15, 120) * mm});
            skCircle(sketch, "E85", {"center": v(0, 120) * mm, "radius": 6 * mm});
            skLineSegment(sketch, "E86", {"start": v(-15, 120) * mm, "end": v(15, 120) * mm, "construction": true});
            skLineSegment(sketch, "E87", {"start": v(-15, 108) * mm, "end": v(15, 108) * mm, "construction": true});
            skLineSegment(sketch, "E88", {"start": v(-80, 0) * mm, "end": v(80, 0) * mm, "construction": true});
            skLineSegment(sketch, "E89.MirrorCS", {"start": v(-15, -120) * mm, "end": v(15, -120) * mm, "construction": true});
            skLineSegment(sketch, "E90.MirrorCS", {"start": v(15, -108) * mm, "end": v(15, -120) * mm});
            skLineSegment(sketch, "E91.MirrorCS", {"start": v(-15, -108) * mm, "end": v(-15, -120) * mm});
            skLineSegment(sketch, "E92.MirrorCS", {"start": v(-15, -108) * mm, "end": v(15, -108) * mm, "construction": true});
            skCircle(sketch, "E93.MirrorC", {"center": v(0, -120) * mm, "radius": 6 * mm});
            skLineSegment(sketch, "E94.MirrorCS", {"start": v(-33, -90) * mm, "end": v(-15, -108) * mm});
            skLineSegment(sketch, "E95.MirrorCS", {"start": v(33, -90) * mm, "end": v(15, -108) * mm});
            skArc(sketch, "E96.MirrorCS", {"start": v(15, -120) * mm, "mid": v(0, -135) * mm, "end": v(-15, -120) * mm});
            skLineSegment(sketch, "E97.MirrorCS", {"start": v(0, -90) * mm, "end": v(0, -110.56) * mm, "construction": true});
            skSolve(sketch);
        }
        {
            var Q0;
            {var subQ1=sQuery(id+"F16.wireOp",EDGE,"E80");Q0=makeQuery(id+"F16.imprint","IMPRINT",FACE,{"disambiguationData":[TD([[makeQuery(id+"F16.imprint","IMPRINT",EDGE,{"derivedFrom":subQ1}),-1.0]])]});}
            var Q1;
            Q1=makeQuery(id+"F16.imprint","IMPRINT",FACE,{"disambiguationData":[TD([[makeQuery(id+"F16.imprint","IMPRINT",EDGE,{"derivedFrom":makeQuery(id+"F1.opExtrude","CAP_EDGE",EDGE,{"disambiguationData":[OSD([sQuery(id+"F0.wireOp",EDGE,"E1.left")])],"isStart":true})}),-1.0]])]});
            var Q2;
            Q2=makeQuery(id+"F16.imprint","IMPRINT",FACE,{"disambiguationData":[TD([[makeQuery(id+"F16.imprint","IMPRINT",EDGE,{"derivedFrom":sQuery(id+"F16.wireOp",EDGE,"E93.MirrorC")}),1.0]])]});
            var Q3;
            Q3=makeQuery(id+"F2.opExtrude","CAP_FACE",FACE,{"disambiguationData":[OSD([sQuery(id+"F0.wireOp",EDGE,"E12"),sQuery(id+"F0.wireOp",EDGE,"E13"),sQuery(id+"F0.wireOp",EDGE,"E14"),sQuery(id+"F0.wireOp",EDGE,"E15"),sQuery(id+"F0.wireOp",EDGE,"E17.filletArc"),sQuery(id+"F0.wireOp",EDGE,"E18.filletArc"),sQuery(id+"F0.wireOp",EDGE,"E19.filletArc"),sQuery(id+"F0.wireOp",EDGE,"E20.filletArc"),sQuery(id+"F0.wireOp",EDGE,"E25.0"),sQuery(id+"F0.wireOp",EDGE,"E25.1"),sQuery(id+"F0.wireOp",EDGE,"E25.2"),sQuery(id+"F0.wireOp",EDGE,"E25.3"),sQuery(id+"F0.wireOp",EDGE,"E25.4"),sQuery(id+"F0.wireOp",EDGE,"E25.5"),sQuery(id+"F0.wireOp",EDGE,"E25.6"),sQuery(id+"F0.wireOp",EDGE,"E25.7")])],"isStart":false});
            extrude(context, id + "F17", {"entities" : qUnion([Q0, Q1, Q2]), "endBound" : BoundingType.UP_TO_SURFACE, "endBoundEntityFace" : qUnion([Q3]), "depth" : 25 * mm});
        }
    });
